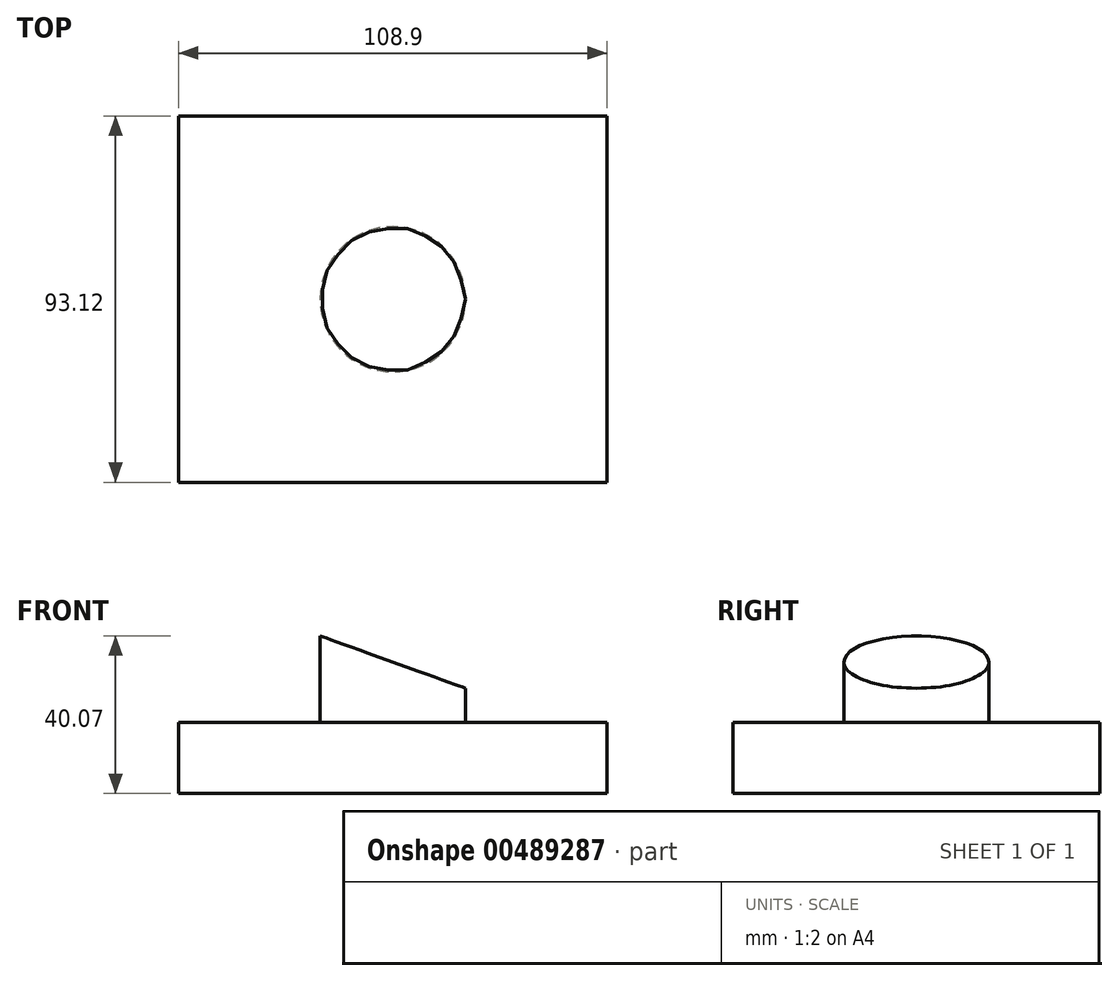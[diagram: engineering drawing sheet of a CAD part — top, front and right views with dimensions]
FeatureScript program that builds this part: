
annotation { "Feature Type Name" : "Feature", "Feature Type Description" : "" }
export const myFeature = defineFeature(function(context is Context, id is Id, definition is map)
    precondition{}
    {
        {
            var Q0;
            Q0=qCreatedBy(makeId("Top.planeOp"),FACE);
            var sketch = newSketch(context, id + "F0", { "sketchPlane" : qUnion([Q0])});
            skLineSegment(sketch, "E0.bottom", {"start": v(54.45, 46.56) * mm, "end": v(-54.45, 46.56) * mm});
            skLineSegment(sketch, "E0.top", {"start": v(54.45, -46.56) * mm, "end": v(-54.45, -46.56) * mm});
            skLineSegment(sketch, "E0.left", {"start": v(54.45, 46.56) * mm, "end": v(54.45, -46.56) * mm});
            skLineSegment(sketch, "E0.right", {"start": v(-54.45, 46.56) * mm, "end": v(-54.45, -46.56) * mm});
            skPoint(sketch, "E0.middle", {"position": v(0, 0) * mm});
            skSolve(sketch);
        }
        {
            var Q0;
            Q0=makeQuery(id+"F0.imprint","IMPRINT",FACE,{"disambiguationData":[TD([[makeQuery(id+"F0.imprint","IMPRINT",EDGE,{"derivedFrom":sQuery(id+"F0.wireOp",EDGE,"E0.bottom")}),1.0]])]});
            extrude(context, id + "F1", {"entities" : qUnion([Q0]), "oppositeDirection" : true, "depth" : 18.03 * mm});
        }
        {
            var Q0;
            Q0=qCreatedBy(makeId("Top.planeOp"),FACE);
            var sketch = newSketch(context, id + "F2", { "sketchPlane" : qUnion([Q0])});
            skCircle(sketch, "E1", {"center": v(0, 0) * mm, "radius": 18.45 * mm});
            skSolve(sketch);
        }
        {
            var Q0;
            Q0=makeQuery(id+"F2.imprint","IMPRINT",FACE,{"disambiguationData":[TD([[makeQuery(id+"F2.imprint","IMPRINT",EDGE,{"derivedFrom":sQuery(id+"F2.wireOp",EDGE,"E1")}),1.0]])]});
            extrude(context, id + "F3", {"entities" : qUnion([Q0]), "operationType" : NewBodyOperationType.ADD, "depth" : 54.6 * mm});
        }
        {
            var Q0;
            Q0=qCreatedBy(makeId("Front.planeOp"),FACE);
            var sketch = newSketch(context, id + "F4", { "sketchPlane" : qUnion([Q0])});
            skLineSegment(sketch, "E2", {"start": v(-27.63, 25.35) * mm, "end": v(42.75, 0) * mm});
            skLineSegment(sketch, "E3", {"start": v(42.75, 25.35) * mm, "end": v(42.75, 0) * mm});
            skLineSegment(sketch, "E4", {"start": v(42.75, 25.35) * mm, "end": v(42.75, 92.52) * mm});
            skLineSegment(sketch, "E5", {"start": v(42.75, 92.52) * mm, "end": v(-27.63, 92.52) * mm});
            skLineSegment(sketch, "E6", {"start": v(-27.63, 92.52) * mm, "end": v(-27.63, 25.35) * mm});
            skSolve(sketch);
        }
        {
            var Q0;
            Q0=makeQuery(id+"F4.imprint","IMPRINT",FACE,{"disambiguationData":[TD([[makeQuery(id+"F4.imprint","IMPRINT",EDGE,{"derivedFrom":sQuery(id+"F4.wireOp",EDGE,"E2")}),1.0]])]});
            extrude(context, id + "F5", {"entities" : qUnion([Q0]), "operationType" : NewBodyOperationType.REMOVE, "endBound" : BoundingType.SYMMETRIC, "oppositeDirection" : true, "depth" : 50.8 * mm});
        }
    });
